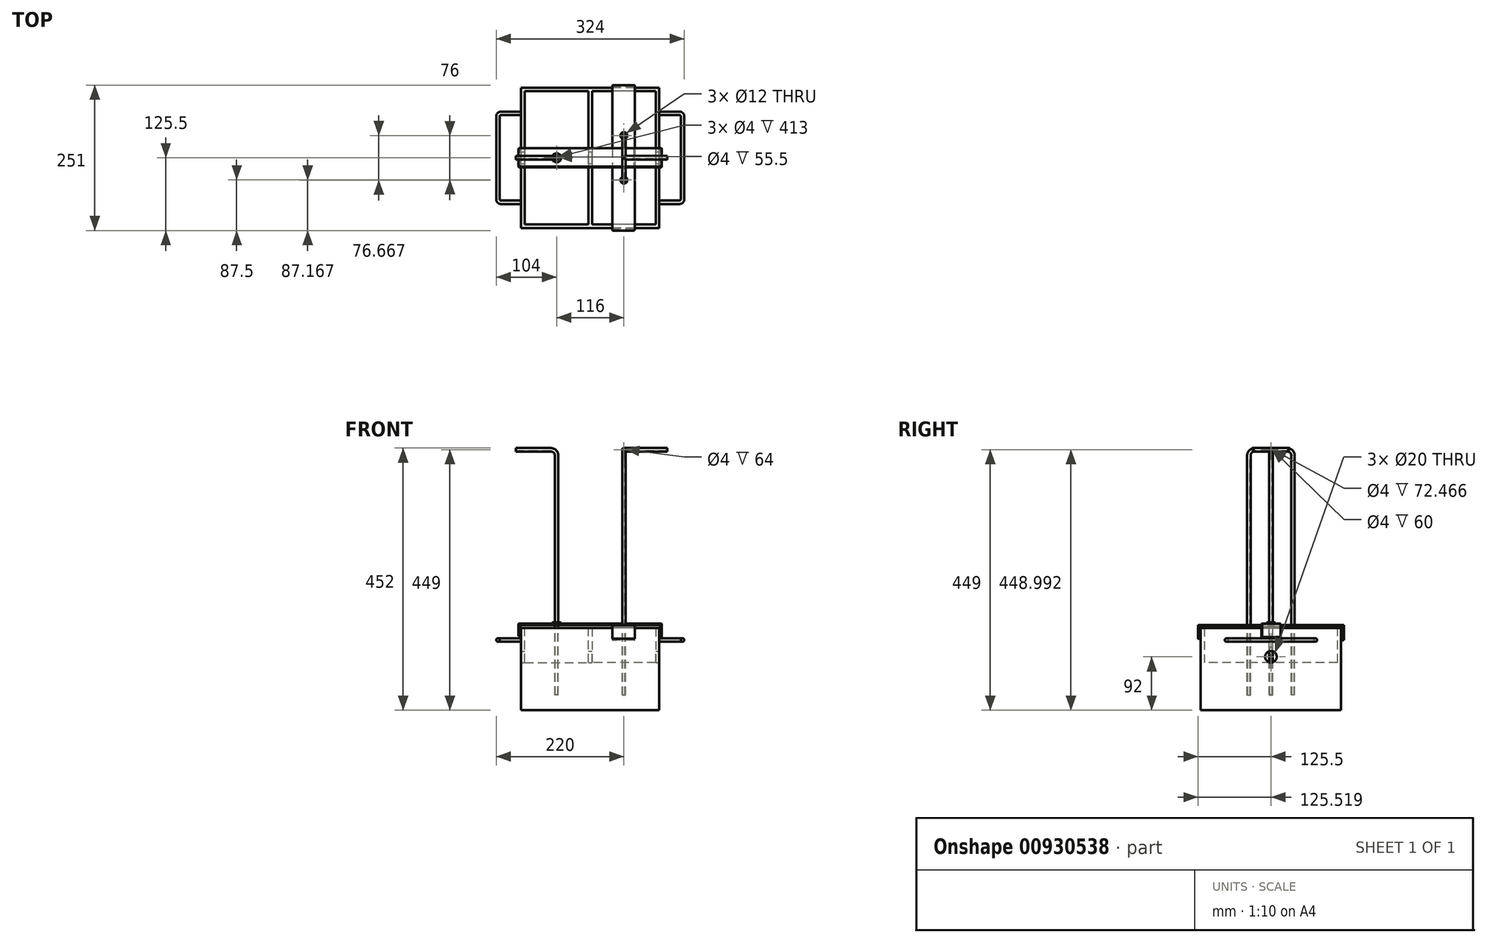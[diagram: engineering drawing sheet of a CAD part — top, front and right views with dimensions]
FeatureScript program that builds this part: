
annotation { "Feature Type Name" : "Feature", "Feature Type Description" : "" }
export const myFeature = defineFeature(function(context is Context, id is Id, definition is map)
    precondition{}
    {
        {
            assignVariable(context, id + "F0", {"name" : "BWidth", "anyValue" : 230});
        }
        {
            assignVariable(context, id + "F1", {"name" : "BLength", "anyValue" : 110});
        }
        {
            assignVariable(context, id + "F2", {"name" : "BHeight", "anyValue" : 76});
        }
        {
            assignVariable(context, id + "F3", {"name" : "SSThick", "anyValue" : 6});
        }
        {
            assignVariable(context, id + "F4", {"name" : "RLevel", "anyValue" : 10});
        }
        {
            var Q0;
            Q0=qCreatedBy(makeId("Right.planeOp"),FACE);
            var sketch = newSketch(context, id + "F5", { "sketchPlane" : qUnion([Q0])});
            skLineSegment(sketch, "E0", {"start": v(0, 0) * mm, "end": v(-242, 0) * mm});
            skLineSegment(sketch, "E1", {"start": v(-242, 0) * mm, "end": v(-242, 142) * mm});
            skLineSegment(sketch, "E2", {"start": v(-242, 142) * mm, "end": v(-236, 142) * mm});
            skLineSegment(sketch, "E3", {"start": v(-236, 142) * mm, "end": v(-236, 6) * mm});
            skLineSegment(sketch, "E4", {"start": v(-236, 6) * mm, "end": v(-6, 6) * mm});
            skLineSegment(sketch, "E5", {"start": v(-6, 6) * mm, "end": v(-6, 142) * mm});
            skLineSegment(sketch, "E6", {"start": v(-6, 142) * mm, "end": v(0, 142) * mm});
            skLineSegment(sketch, "E7", {"start": v(0, 142) * mm, "end": v(0, 0) * mm});
            skLineSegment(sketch, "E8", {"start": v(0, 47.24) * mm, "end": v(0, 0) * mm, "construction": true});
            skSolve(sketch);
        }
        {
            var Q0;
            Q0=makeQuery(id+"F5.imprint","IMPRINT",FACE,{"disambiguationData":[TD([[makeQuery(id+"F5.imprint","IMPRINT",EDGE,{"derivedFrom":sQuery(id+"F5.wireOp",EDGE,"E7")}),1.0]])]});
            var Q1;
            Q1=makeQuery(id+"F5.imprint","IMPRINT",FACE,{"disambiguationData":[TD([[makeQuery(id+"F5.imprint","IMPRINT",EDGE,{"derivedFrom":sQuery(id+"F5.wireOp",EDGE,"E0")}),-1.0]])]});
            extrude(context, id + "F6", {"entities" : qUnion([Q0, Q1]), "depth" : (getVariable(context, 'BLength') + 0.5 * getVariable(context, 'SSThick')) * mm, "offsetDistance" : 25 * mm});
        }
        {
            var Q0;
            Q0=qCreatedBy(makeId("Right.planeOp"),FACE);
            var sketch = newSketch(context, id + "F7", { "sketchPlane" : qUnion([Q0])});
            skLineSegment(sketch, "E9.bottom", {"start": v(0, 142) * mm, "end": v(-242, 142) * mm});
            skLineSegment(sketch, "E9.top", {"start": v(0, 0) * mm, "end": v(-242, 0) * mm});
            skLineSegment(sketch, "E9.left", {"start": v(0, 142) * mm, "end": v(0, 0) * mm});
            skLineSegment(sketch, "E9.right", {"start": v(-242, 142) * mm, "end": v(-242, 0) * mm});
            skPoint(sketch, "E10", {"position": v(0, 123) * mm});
            skLineSegment(sketch, "E11", {"start": v(-121, 148.37) * mm, "end": v(-121, -16.63) * mm, "construction": true});
            skPoint(sketch, "E11.startSnap0", {"position": v(-121, 142) * mm});
            skPoint(sketch, "E11.endSnap0", {"position": v(-121, 0) * mm});
            skSolve(sketch);
        }
        {
            var Q0;
            Q0 = qSketchRegion(id + "F7", true);
            extrude(context, id + "F8", {"entities" : qUnion([Q0]), "operationType" : NewBodyOperationType.ADD, "depth" : (0.5 * getVariable(context, 'SSThick')) * mm, "offsetDistance" : 25 * mm});
        }
        {
            var Q0;
            Q0=makeQuery(id+"F6.opExtrude","SWEPT_BODY",BODY,{"disambiguationData":[OSD([sQuery(id+"F5.wireOp",EDGE,"E0"),sQuery(id+"F5.wireOp",EDGE,"E1"),sQuery(id+"F5.wireOp",EDGE,"E2"),sQuery(id+"F5.wireOp",EDGE,"E3"),sQuery(id+"F5.wireOp",EDGE,"E4"),sQuery(id+"F5.wireOp",EDGE,"E5"),sQuery(id+"F5.wireOp",EDGE,"E6"),sQuery(id+"F5.wireOp",EDGE,"af327641-4c30-46ca-b10d-6913c187e19a0.MirrorCS"),sQuery(id+"F5.wireOp",EDGE,"cdb5822d-f6a7-44e6-b872-cb7c605309c70.MirrorCS"),sQuery(id+"F5.wireOp",EDGE,"ea72e5ea-b274-412d-a60d-40bec931ebde0.MirrorCS"),sQuery(id+"F5.wireOp",EDGE,"cc1766e8-4033-44cc-bf69-035f61d04cb70.MirrorCS"),sQuery(id+"F5.wireOp",EDGE,"c6e5a0e8-dc4d-418c-873e-d246f6d1d2250.MirrorCS"),sQuery(id+"F5.wireOp",EDGE,"a5024cb1-cd79-4f41-9afd-c9afbaccf6ca0.MirrorCS"),sQuery(id+"F5.wireOp",EDGE,"9c3db3c7-590e-4d40-8187-3b4e1b05696b0.MirrorCS")])]});
            var Q1;
            Q1=qCreatedBy(makeId("Right.planeOp"),FACE);
            mirror(context, id + "F9", {"operationType" : NewBodyOperationType.ADD, "entities" : qUnion([Q0]), "mirrorPlane" : qUnion([Q1])});
        }
        {
            var Q0;
            Q0=qCreatedBy(makeId("Front.planeOp"),FACE);
            var sketch = newSketch(context, id + "F10", { "sketchPlane" : qUnion([Q0])});
            skLineSegment(sketch, "E12.top", {"start": v(-113, 0) * mm, "end": v(-119, 0) * mm});
            skLineSegment(sketch, "E12.left", {"start": v(-113, 142) * mm, "end": v(-113, 0) * mm});
            skLineSegment(sketch, "E12.right", {"start": v(-119, 142) * mm, "end": v(-119, 0) * mm});
            skLineSegment(sketch, "E13.bottom", {"start": v(113, 142) * mm, "end": v(119, 142) * mm});
            skLineSegment(sketch, "E13.top", {"start": v(113, 0) * mm, "end": v(119, 0) * mm});
            skLineSegment(sketch, "E13.left", {"start": v(113, 142) * mm, "end": v(113, 0) * mm});
            skLineSegment(sketch, "E13.right", {"start": v(119, 142) * mm, "end": v(119, 0) * mm});
            skLineSegment(sketch, "E14", {"start": v(-119, 142) * mm, "end": v(-113, 142) * mm});
            skSolve(sketch);
        }
        {
            var Q0;
            Q0=makeQuery(id+"F10.imprint","IMPRINT",FACE,{"disambiguationData":[TD([[makeQuery(id+"F10.imprint","IMPRINT",EDGE,{"derivedFrom":sQuery(id+"F10.wireOp",EDGE,"E13.bottom")}),-1.0]])]});
            var Q1;
            Q1=makeQuery(id+"F10.imprint","IMPRINT",FACE,{"disambiguationData":[TD([[makeQuery(id+"F10.imprint","IMPRINT",EDGE,{"derivedFrom":sQuery(id+"F10.wireOp",EDGE,"E12.top")}),-1.0]])]});
            extrude(context, id + "F11", {"entities" : qUnion([Q0, Q1]), "operationType" : NewBodyOperationType.ADD, "depth" : (getVariable(context, 'BWidth') + 2 * getVariable(context, 'SSThick')) * mm, "offsetDistance" : 25 * mm});
        }
        {
            var Q0;
            Q0=makeQuery(id+"F11.opExtrude","SWEPT_FACE",FACE,{"disambiguationData":[OSD([sQuery(id+"F10.wireOp",EDGE,"E13.right")])]});
            var sketch = newSketch(context, id + "F12", { "sketchPlane" : qUnion([Q0])});
            skLineSegment(sketch, "E15", {"start": v(-121, 186.02) * mm, "end": v(-121, -14.5) * mm, "construction": true});
            skLineSegment(sketch, "E16", {"start": v(-127.49, 92) * mm, "end": v(39.18, 92) * mm, "construction": true});
            skCircle(sketch, "E17", {"center": v(-121, 92) * mm, "radius": 10 * mm});
            skSolve(sketch);
        }
        {
            var Q0;
            Q0=makeQuery(id+"F12.imprint","IMPRINT",FACE,{"disambiguationData":[TD([[makeQuery(id+"F12.imprint","IMPRINT",EDGE,{"derivedFrom":sQuery(id+"F12.wireOp",EDGE,"E17")}),1.0]])]});
            var Q1;
            Q1=sQuery(id+"F12.wireOp",EDGE,"E17");
            extrude(context, id + "F13", {"entities" : qUnion([Q0]), "operationType" : NewBodyOperationType.REMOVE, "surfaceEntities" : qUnion([Q1]), "endBound" : BoundingType.THROUGH_ALL, "oppositeDirection" : true, "depth" : 25 * mm, "offsetDistance" : 25 * mm});
        }
        {
            var Q0;
            Q0=qCreatedBy(makeId("Top.planeOp"),FACE);
            cPlane(context, id + "F14", {"entities" : qUnion([Q0]), "cplaneType" : CPlaneType.OFFSET, "offset" : (getVariable(context, 'BHeight') + 2 * getVariable(context, 'RLevel') + 0.5 * 50) * mm, "width" : 150 * mm, "height" : 150 * mm});
        }
        {
            var Q0;
            Q0=qCreatedBy(id+"F14.planeOp",FACE);
            var sketch = newSketch(context, id + "F15", { "sketchPlane" : qUnion([Q0])});
            skLineSegment(sketch, "E18", {"start": v(-133.66, -121) * mm, "end": v(154.72, -121) * mm, "construction": true});
            skLineSegment(sketch, "E19", {"start": v(119, -44.33) * mm, "end": v(154, -44.33) * mm});
            skLineSegment(sketch, "E20", {"start": v(159, -49.33) * mm, "end": v(159, -192.67) * mm});
            skLineSegment(sketch, "E21", {"start": v(154, -197.67) * mm, "end": v(119, -197.67) * mm});
            skPoint(sketch, "E22.visualSharp", {"position": v(159, -44.33) * mm});
            skArc(sketch, "E22.filletArc", {"start": v(159, -49.33) * mm, "mid": v(157.54, -45.8) * mm, "end": v(154, -44.33) * mm});
            skPoint(sketch, "E23.visualSharp", {"position": v(159, -197.67) * mm});
            skArc(sketch, "E23.filletArc", {"start": v(154, -197.67) * mm, "mid": v(157.54, -196.2) * mm, "end": v(159, -192.67) * mm});
            skSolve(sketch);
        }
        {
            var Q0;
            Q0=makeQuery(id+"F11.opExtrude","SWEPT_FACE",FACE,{"disambiguationData":[OSD([sQuery(id+"F10.wireOp",EDGE,"E13.right")])]});
            var sketch = newSketch(context, id + "F16", { "sketchPlane" : qUnion([Q0])});
            skLineSegment(sketch, "E24", {"start": v(4.97, 121) * mm, "end": v(-102.6, 121) * mm, "construction": true});
            skLineSegment(sketch, "E25", {"start": v(-44.33, 184.58) * mm, "end": v(-44.33, 116.45) * mm, "construction": true});
            skLineSegment(sketch, "E26", {"start": v(-197.67, 183.78) * mm, "end": v(-197.67, 116.45) * mm, "construction": true});
            skCircle(sketch, "E27", {"center": v(-44.33, 121) * mm, "radius": 3 * mm});
            skSolve(sketch);
        }
        {
            var Q0;
            Q0=makeQuery(id+"F16.imprint","IMPRINT",FACE,{"disambiguationData":[TD([[makeQuery(id+"F16.imprint","IMPRINT",EDGE,{"derivedFrom":sQuery(id+"F16.wireOp",EDGE,"E27")}),1.0]])]});
            var Q1;
            Q1=sQuery(id+"F16.wireOp",EDGE,"E27");
            var Q2;
            Q2=sQuery(id+"F15.wireOp",EDGE,"E19");
            var Q3;
            Q3=sQuery(id+"F15.wireOp",EDGE,"E22.filletArc");
            var Q4;
            Q4=sQuery(id+"F15.wireOp",EDGE,"E20");
            var Q5;
            Q5=sQuery(id+"F15.wireOp",EDGE,"E23.filletArc");
            var Q6;
            Q6=sQuery(id+"F15.wireOp",EDGE,"E21");
            sweep(context, id + "F17", {"profiles" : qUnion([Q0]), "surfaceProfiles" : qUnion([Q1]), "path" : qUnion([Q2, Q3, Q4, Q5, Q6])});
        }
        {
            var Q0;
            Q0=makeQuery(id+"F17.opSweep","SWEPT_BODY",BODY,{"disambiguationData":[OSD([sQuery(id+"F15.wireOp",EDGE,"E21"),sQuery(id+"F16.wireOp",EDGE,"E27")])]});
            var Q1;
            Q1=qCreatedBy(makeId("Right.planeOp"),FACE);
            mirror(context, id + "F18", {"entities" : qUnion([Q0]), "mirrorPlane" : qUnion([Q1])});
        }
        {
            var Q0;
            Q0=makeQuery(id+"F8.opExtrude","CAP_FACE",FACE,{"disambiguationData":[OSD([sQuery(id+"F7.wireOp",EDGE,"E9.bottom"),sQuery(id+"F7.wireOp",EDGE,"E9.top"),sQuery(id+"F7.wireOp",EDGE,"E9.left"),sQuery(id+"F7.wireOp",EDGE,"E9.right")])],"isStart":false});
            var sketch = newSketch(context, id + "F19", { "sketchPlane" : qUnion([Q0])});
            skLineSegment(sketch, "E28", {"start": v(-236, 6) * mm, "end": v(-6, 6) * mm});
            skLineSegment(sketch, "E29", {"start": v(-6, 6) * mm, "end": v(-6, 82) * mm});
            skLineSegment(sketch, "E30", {"start": v(-6, 82) * mm, "end": v(-236, 82) * mm});
            skLineSegment(sketch, "E31", {"start": v(-236, 82) * mm, "end": v(-236, 6) * mm});
            skSolve(sketch);
        }
        {
            var Q0;
            Q0=makeQuery(id+"F19.imprint","IMPRINT",FACE,{"disambiguationData":[TD([[makeQuery(id+"F19.imprint","IMPRINT",EDGE,{"derivedFrom":sQuery(id+"F19.wireOp",EDGE,"E28")}),1.0]])]});
            extrude(context, id + "F20", {"entities" : qUnion([Q0]), "depth" : (getVariable(context, 'BLength')) * mm, "offsetDistance" : 25 * mm});
        }
        {
            var Q0;
            Q0=makeQuery(id+"F20.opExtrude","SWEPT_BODY",BODY,{"disambiguationData":[OSD([sQuery(id+"F19.wireOp",EDGE,"E28"),sQuery(id+"F19.wireOp",EDGE,"E29"),sQuery(id+"F19.wireOp",EDGE,"E30"),sQuery(id+"F19.wireOp",EDGE,"E31")])]});
            var Q1;
            Q1=qCreatedBy(makeId("Right.planeOp"),FACE);
            mirror(context, id + "F21", {"operationType" : NewBodyOperationType.ADD, "entities" : qUnion([Q0]), "mirrorPlane" : qUnion([Q1])});
        }
        {
            var Q0;
            {var subQ0=makeQuery(id+"F8.boolean.opBoolean","MERGE",FACE,{"derivedFrom":[makeQuery(id+"F6.opExtrude","SWEPT_FACE",FACE,{"disambiguationData":[OSD([sQuery(id+"F5.wireOp",EDGE,"E2")])]}),makeQuery(id+"F6.opExtrude","SWEPT_FACE",FACE,{"disambiguationData":[OSD([sQuery(id+"F5.wireOp",EDGE,"E6")])]}),makeQuery(id+"F8.opExtrude","SWEPT_FACE",FACE,{"disambiguationData":[OSD([sQuery(id+"F7.wireOp",EDGE,"E9.bottom")])]})]});Q0=makeQuery(id+"F11.boolean.opBoolean","MERGE",FACE,{"derivedFrom":[makeQuery(id+"F9.boolean.opBoolean","MERGE",FACE,{"derivedFrom":[subQ0,makeQuery(id+"F9.opPattern","COPY",FACE,{"derivedFrom":subQ0,"instanceName":"1"})]}),makeQuery(id+"F11.opExtrude","SWEPT_FACE",FACE,{"disambiguationData":[OSD([sQuery(id+"F10.wireOp",EDGE,"E13.bottom")])]}),makeQuery(id+"F11.opExtrude","SWEPT_FACE",FACE,{"disambiguationData":[OSD([sQuery(id+"F10.wireOp",EDGE,"E14")])]})]});}
            var sketch = newSketch(context, id + "F22", { "sketchPlane" : qUnion([Q0])});
            skLineSegment(sketch, "E32", {"start": v(-134.05, -121) * mm, "end": v(132.86, -121) * mm, "construction": true});
            skPoint(sketch, "E32.startSnap0", {"position": v(-119, -121) * mm});
            skLineSegment(sketch, "E33", {"start": v(-58, 11.94) * mm, "end": v(-58, -251.2) * mm, "construction": true});
            skPoint(sketch, "E33.startSnap0", {"position": v(-58, -6) * mm});
            skLineSegment(sketch, "E34", {"start": v(58, 25.69) * mm, "end": v(58, -276.75) * mm, "construction": true});
            skLineSegment(sketch, "E35", {"start": v(138.24, -82.67) * mm, "end": v(-35.44, -82.67) * mm, "construction": true});
            skLineSegment(sketch, "E36", {"start": v(-28.7, -159.33) * mm, "end": v(137.49, -159.33) * mm, "construction": true});
            skCircle(sketch, "E37", {"center": v(58, -159.33) * mm, "radius": 6 * mm});
            skCircle(sketch, "E38", {"center": v(58, -82.67) * mm, "radius": 6 * mm});
            skCircle(sketch, "E39", {"center": v(-58, -121) * mm, "radius": 6 * mm});
            skSolve(sketch);
        }
        {
            var Q0;
            Q0=qCreatedBy(makeId("Right.planeOp"),FACE);
            var Q1;
            Q1=sQuery(id+"F22.wireOp",VERTEX,"E38.center");
            cPlane(context, id + "F23", {"entities" : qUnion([Q0, Q1]), "cplaneType" : CPlaneType.PLANE_POINT, "offset" : (getVariable(context, 'BLength') / 2 + 0.5 * getVariable(context, 'SSThick')) * mm, "oppositeDirection" : true, "width" : 150 * mm, "height" : 150 * mm});
        }
        {
            var Q0;
            Q0=qCreatedBy(id+"F23.planeOp",FACE);
            var sketch = newSketch(context, id + "F24", { "sketchPlane" : qUnion([Q0])});
            skLineSegment(sketch, "E40", {"start": v(-245, 122) * mm, "end": v(-245, 145) * mm});
            skLineSegment(sketch, "E41", {"start": v(-245, 145) * mm, "end": v(3, 145) * mm});
            skLineSegment(sketch, "E42", {"start": v(3, 145) * mm, "end": v(3, 122) * mm});
            skSolve(sketch);
        }
        {
            var Q0;
            Q0=qCreatedBy(id+"F14.planeOp",FACE);
            var sketch = newSketch(context, id + "F25", { "sketchPlane" : qUnion([Q0])});
            skLineSegment(sketch, "E43", {"start": v(75.14, 1.5) * mm, "end": v(45.14, 1.5) * mm});
            skLineSegment(sketch, "E44", {"start": v(75.14, 4.5) * mm, "end": v(38.33, 4.5) * mm});
            skArc(sketch, "E45", {"start": v(75.14, 1.5) * mm, "mid": v(76.64, 3) * mm, "end": v(75.14, 4.5) * mm});
            skArc(sketch, "E46", {"start": v(45.14, 1.5) * mm, "mid": v(41.42, 2.28) * mm, "end": v(38.33, 4.5) * mm});
            skSolve(sketch);
        }
        {
            var Q0;
            Q0=makeQuery(id+"F25.imprint","IMPRINT",FACE,{"disambiguationData":[TD([[makeQuery(id+"F25.imprint","IMPRINT",EDGE,{"derivedFrom":sQuery(id+"F25.wireOp",EDGE,"E43")}),-1.0]])]});
            var Q1;
            Q1=sQuery(id+"F24.wireOp",EDGE,"E42");
            var Q2;
            Q2=sQuery(id+"F24.wireOp",EDGE,"E41");
            var Q3;
            Q3=sQuery(id+"F24.wireOp",EDGE,"E40");
            sweep(context, id + "F26", {"profiles" : qUnion([Q0]), "path" : qUnion([Q1, Q2, Q3])});
        }
        {
            var Q0;
            Q0=qCreatedBy(makeId("Front.planeOp"),FACE);
            var Q1;
            Q1=sQuery(id+"F22.wireOp",VERTEX,"E39.center");
            cPlane(context, id + "F27", {"entities" : qUnion([Q0, Q1]), "cplaneType" : CPlaneType.PLANE_POINT, "offset" : (getVariable(context, 'BWidth') / 6) * mm, "width" : 150 * mm, "height" : 150 * mm});
        }
        {
            var Q0;
            Q0=qCreatedBy(id+"F27.planeOp",FACE);
            var sketch = newSketch(context, id + "F28", { "sketchPlane" : qUnion([Q0])});
            skLineSegment(sketch, "E47", {"start": v(-122, 127) * mm, "end": v(-122, 148) * mm});
            skLineSegment(sketch, "E48", {"start": v(-122, 148) * mm, "end": v(122, 148) * mm});
            skLineSegment(sketch, "E49", {"start": v(122, 148) * mm, "end": v(122, 127) * mm});
            skSolve(sketch);
        }
        {
            var Q0;
            Q0=qCreatedBy(id+"F14.planeOp",FACE);
            cPlane(context, id + "F29", {"entities" : qUnion([Q0]), "cplaneType" : CPlaneType.OFFSET, "offset" : 5 * mm, "width" : 150 * mm, "height" : 150 * mm});
        }
        {
            var Q0;
            Q0=qCreatedBy(id+"F29.planeOp",FACE);
            var sketch = newSketch(context, id + "F30", { "sketchPlane" : qUnion([Q0])});
            skLineSegment(sketch, "E50", {"start": v(120.5, -135.9) * mm, "end": v(120.5, -105.9) * mm});
            skLineSegment(sketch, "E51", {"start": v(123.5, -136) * mm, "end": v(123.5, -105.9) * mm});
            skArc(sketch, "E52", {"start": v(120.5, -135.9) * mm, "mid": v(121.95, -137.4) * mm, "end": v(123.5, -136) * mm});
            skArc(sketch, "E53", {"start": v(123.5, -105.9) * mm, "mid": v(122, -104.4) * mm, "end": v(120.5, -105.9) * mm});
            skSolve(sketch);
        }
        {
            var Q0;
            Q0=makeQuery(id+"F30.imprint","IMPRINT",FACE,{"disambiguationData":[TD([[makeQuery(id+"F30.imprint","IMPRINT",EDGE,{"derivedFrom":sQuery(id+"F30.wireOp",EDGE,"E50")}),-1.0]])]});
            var Q1;
            Q1=sQuery(id+"F28.wireOp",EDGE,"E49");
            var Q2;
            Q2=sQuery(id+"F28.wireOp",EDGE,"E48");
            var Q3;
            Q3=sQuery(id+"F28.wireOp",EDGE,"E47");
            sweep(context, id + "F31", {"operationType" : NewBodyOperationType.ADD, "profiles" : qUnion([Q0]), "path" : qUnion([Q1, Q2, Q3])});
        }
        {
            var Q0;
            Q0=sQuery(id+"F22.wireOp",VERTEX,"E39.center");
            var Q1;
            Q1=sQuery(id+"F22.wireOp",VERTEX,"E38.center");
            var Q2;
            Q2=sQuery(id+"F22.wireOp",VERTEX,"E37.center");
            var Q3;
            Q3=makeQuery(id+"F26.opSweep","SWEPT_BODY",BODY,{"disambiguationData":[OSD([sQuery(id+"F24.wireOp",EDGE,"E40"),sQuery(id+"F25.wireOp",EDGE,"E43"),sQuery(id+"F25.wireOp",EDGE,"E44"),sQuery(id+"F25.wireOp",EDGE,"E45"),sQuery(id+"F25.wireOp",EDGE,"E46")])]});
            hole(context, id + "F32", {"style" : HoleStyle.SIMPLE, "endStyle" : HoleEndStyle.THROUGH, "oppositeDirection" : true, "standardTappedOrClearance" : lookupTablePath({ "standard" : "ISO", "size" : "12", "type" : "Drilled" }), "standardBlindInLast" : lookupTablePath({ "standard" : "ISO", "size" : "12", "type" : "Drilled" }), "holeDiameter" : 12 * mm, "majorDiameter" : 5 * mm, "isTappedThrough" : true, "tappedDepth" : 12 * mm, "tapClearance" : 3, "startFromSketch" : true, "locations" : qUnion([Q0, Q1, Q2]), "scope" : qUnion([Q3])});
        }
        {
            var Q0;
            Q0=makeQuery(id+"F31.opSweep","SWEPT_FACE",FACE,{"disambiguationData":[OSD([sQuery(id+"F28.wireOp",EDGE,"E48"),sQuery(id+"F30.wireOp",EDGE,"E51")])]});
            var sketch = newSketch(context, id + "F33", { "sketchPlane" : qUnion([Q0])});
            skCircle(sketch, "E54", {"center": v(-58, -121) * mm, "radius": 3 * mm});
            skCircle(sketch, "E55", {"center": v(-58, -121) * mm, "radius": 2 * mm});
            skSolve(sketch);
        }
        {
            var Q0;
            Q0=qCreatedBy(id+"F27.planeOp",FACE);
            var sketch = newSketch(context, id + "F34", { "sketchPlane" : qUnion([Q0])});
            skLineSegment(sketch, "E56", {"start": v(-58, 26) * mm, "end": v(-58, 439) * mm});
            skLineSegment(sketch, "E57", {"start": v(-68, 449) * mm, "end": v(-128, 449) * mm});
            skPoint(sketch, "E58.visualSharp", {"position": v(-58, 449) * mm});
            skArc(sketch, "E58.filletArc", {"start": v(-58, 439) * mm, "mid": v(-60.93, 446.07) * mm, "end": v(-68, 449) * mm});
            skLineSegment(sketch, "E59", {"start": v(-61, 150.08) * mm, "end": v(-65.71, 150.08) * mm});
            skLineSegment(sketch, "E60", {"start": v(-65.71, 150.08) * mm, "end": v(-65.71, 151.08) * mm});
            skLineSegment(sketch, "E61", {"start": v(-65.71, 151.08) * mm, "end": v(-61, 151.08) * mm});
            skLineSegment(sketch, "E62", {"start": v(-61, 151.08) * mm, "end": v(-61, 150.08) * mm});
            skSolve(sketch);
        }
        {
            var Q0;
            Q0=makeQuery(id+"F33.imprint","IMPRINT",FACE,{"disambiguationData":[TD([[makeQuery(id+"F33.imprint","IMPRINT",EDGE,{"derivedFrom":sQuery(id+"F33.wireOp",EDGE,"E54")}),1.0]])]});
            var Q1;
            Q1=sQuery(id+"F34.wireOp",EDGE,"E56");
            var Q2;
            Q2=sQuery(id+"F34.wireOp",EDGE,"E58.filletArc");
            var Q3;
            Q3=sQuery(id+"F34.wireOp",EDGE,"E57");
            sweep(context, id + "F35", {"profiles" : qUnion([Q0]), "path" : qUnion([Q1, Q2, Q3])});
        }
        {
            var Q0;
            Q0=makeQuery(id+"F33.imprint","IMPRINT",FACE,{"disambiguationData":[TD([[makeQuery(id+"F33.imprint","IMPRINT",EDGE,{"derivedFrom":sQuery(id+"F33.wireOp",EDGE,"E55")}),1.0]])]});
            extrude(context, id + "F36", {"entities" : qUnion([Q0]), "operationType" : NewBodyOperationType.REMOVE, "oppositeDirection" : true, "depth" : 123 * mm, "offsetDistance" : 25 * mm});
        }
        {
            var Q0;
            Q0=makeQuery(id+"F35.opSweep","SWEPT_BODY",BODY,{"disambiguationData":[OSD([sQuery(id+"F33.wireOp",EDGE,"E54"),sQuery(id+"F33.wireOp",EDGE,"E55"),sQuery(id+"F34.wireOp",EDGE,"E57")])]});
            transform(context, id + "F37", {"entities" : qUnion([Q0]), "transformType" : TransformType.TRANSLATION_3D, "dx" : 116 * mm, "dy" : 38 * mm, "dz" : 0 * mm, "makeCopy" : true});
        }
        {
            var Q0;
            Q0=makeQuery(id+"F35.opSweep","SWEPT_BODY",BODY,{"disambiguationData":[OSD([sQuery(id+"F33.wireOp",EDGE,"E54"),sQuery(id+"F33.wireOp",EDGE,"E55"),sQuery(id+"F34.wireOp",EDGE,"E57")])]});
            transform(context, id + "F38", {"entities" : qUnion([Q0]), "transformType" : TransformType.TRANSLATION_3D, "dx" : 116 * mm, "dy" : -38 * mm, "dz" : 0 * mm, "makeCopy" : true});
        }
        {
            var Q0;
            Q0=makeQuery(id+"F37.opPattern","COPY",FACE,{"derivedFrom":makeQuery(id+"F35.opSweep","CAP_FACE",FACE,{"disambiguationData":[OSD([sQuery(id+"F33.wireOp",EDGE,"E54"),sQuery(id+"F33.wireOp",EDGE,"E55"),sQuery(id+"F34.wireOp",VERTEX,"E57.end")])],"isStart":false}),"instanceName":"1"});
            var sketch = newSketch(context, id + "F39", { "sketchPlane" : qUnion([Q0])});
            skLineSegment(sketch, "E63", {"start": v(83, 449) * mm, "end": v(159, 449) * mm, "construction": true});
            skSolve(sketch);
        }
        {
            var Q0;
            {var subQ6=makeQuery(id+"F8.opExtrude","CAP_EDGE",EDGE,{"disambiguationData":[OSD([sQuery(id+"F7.wireOp",EDGE,"E9.bottom")])],"isStart":false});Q0=makeQuery(id+"F22.imprint","IMPRINT",FACE,{"disambiguationData":[TD([[makeQuery(id+"F22.imprint","IMPRINT",EDGE,{"derivedFrom":subQ6}),-1.0]])]});}
            var Q1;
            Q1=sQuery(id+"F39.wireOp",VERTEX,"E63.start");
            cPlane(context, id + "F40", {"entities" : qUnion([Q0, Q1]), "cplaneType" : CPlaneType.PLANE_POINT, "offset" : 25 * mm, "width" : 150 * mm, "height" : 150 * mm});
        }
        {
            var Q0;
            Q0=makeQuery(id+"F37.opPattern","COPY",BODY,{"derivedFrom":makeQuery(id+"F35.opSweep","SWEPT_BODY",BODY,{"disambiguationData":[OSD([sQuery(id+"F33.wireOp",EDGE,"E54"),sQuery(id+"F33.wireOp",EDGE,"E55"),sQuery(id+"F34.wireOp",EDGE,"E57")])]}),"instanceName":"1"});
            var Q1;
            Q1=makeQuery(id+"F37.opPattern","COPY",FACE,{"derivedFrom":makeQuery(id+"F35.opSweep","SWEPT_FACE",FACE,{"disambiguationData":[OSD([sQuery(id+"F33.wireOp",EDGE,"E54"),sQuery(id+"F34.wireOp",EDGE,"E56")])]}),"instanceName":"1"});
            transform(context, id + "F41", {"entities" : qUnion([Q0]), "transformType" : TransformType.ROTATION, "transformAxis" : qUnion([Q1]), "angle" : 90 * degree, "makeCopy" : false});
        }
        {
            var Q0;
            Q0=makeQuery(id+"F38.opPattern","COPY",BODY,{"derivedFrom":makeQuery(id+"F35.opSweep","SWEPT_BODY",BODY,{"disambiguationData":[OSD([sQuery(id+"F33.wireOp",EDGE,"E54"),sQuery(id+"F33.wireOp",EDGE,"E55"),sQuery(id+"F34.wireOp",EDGE,"E57")])]}),"instanceName":"1"});
            var Q1;
            Q1=makeQuery(id+"F38.opPattern","COPY",FACE,{"derivedFrom":makeQuery(id+"F35.opSweep","SWEPT_FACE",FACE,{"disambiguationData":[OSD([sQuery(id+"F33.wireOp",EDGE,"E54"),sQuery(id+"F34.wireOp",EDGE,"E56")])]}),"instanceName":"1"});
            transform(context, id + "F42", {"entities" : qUnion([Q0]), "transformType" : TransformType.ROTATION, "transformAxis" : qUnion([Q1]), "angle" : 270 * degree, "makeCopy" : false});
        }
        {
            var Q0;
            Q0=qCreatedBy(id+"F40.planeOp",FACE);
            var sketch = newSketch(context, id + "F43", { "sketchPlane" : qUnion([Q0])});
            skLineSegment(sketch, "E64", {"start": v(57.94, -121.17) * mm, "end": v(132.7, -121.17) * mm});
            skSolve(sketch);
        }
        {
            var Q0;
            Q0=makeQuery(id+"F35.opSweep","CAP_FACE",FACE,{"disambiguationData":[OSD([sQuery(id+"F33.wireOp",EDGE,"E54"),sQuery(id+"F33.wireOp",EDGE,"E55"),sQuery(id+"F34.wireOp",VERTEX,"E57.end")])],"isStart":false});
            cPlane(context, id + "F44", {"entities" : qUnion([Q0]), "cplaneType" : CPlaneType.OFFSET, "offset" : 250 * mm, "oppositeDirection" : true, "width" : 150 * mm, "height" : 150 * mm});
        }
        {
            var Q0;
            Q0=qCreatedBy(id+"F44.planeOp",FACE);
            var sketch = newSketch(context, id + "F45", { "sketchPlane" : qUnion([Q0])});
            skCircle(sketch, "E65", {"center": v(120.98, 449) * mm, "radius": 2 * mm});
            skCircle(sketch, "E66", {"center": v(120.98, 449) * mm, "radius": 3 * mm});
            skSolve(sketch);
        }
        {
            var Q0;
            Q0=makeQuery(id+"F45.imprint","IMPRINT",FACE,{"disambiguationData":[TD([[makeQuery(id+"F45.imprint","IMPRINT",EDGE,{"derivedFrom":sQuery(id+"F45.wireOp",EDGE,"E65")}),-1.0]])]});
            var Q1;
            Q1=sQuery(id+"F43.wireOp",EDGE,"E64");
            sweep(context, id + "F46", {"operationType" : NewBodyOperationType.ADD, "profiles" : qUnion([Q0]), "path" : qUnion([Q1])});
        }
        {
            var Q0;
            Q0=sQuery(id+"F34.wireOp",EDGE,"E59");
            extrude(context, id + "F47", {"bodyType" : ToolBodyType.SURFACE, "surfaceEntities" : qUnion([Q0]), "depth" : 2 * mm, "offsetDistance" : 25 * mm});
        }
        {
            var Q0;
            Q0=makeQuery(id+"F34.imprint","IMPRINT",FACE,{"disambiguationData":[TD([[makeQuery(id+"F34.imprint","IMPRINT",EDGE,{"derivedFrom":sQuery(id+"F34.wireOp",EDGE,"E59")}),-1.0]])]});
            var Q1;
            Q1=sQuery(id+"F34.wireOp",EDGE,"E56");
            revolve(context, id + "F48", {"operationType" : NewBodyOperationType.ADD, "surfaceOperationType" : NewSurfaceOperationType.NEW, "entities" : qUnion([Q0]), "axis" : qUnion([Q1]), "revolveType" : RevolveType.FULL});
        }
    });
